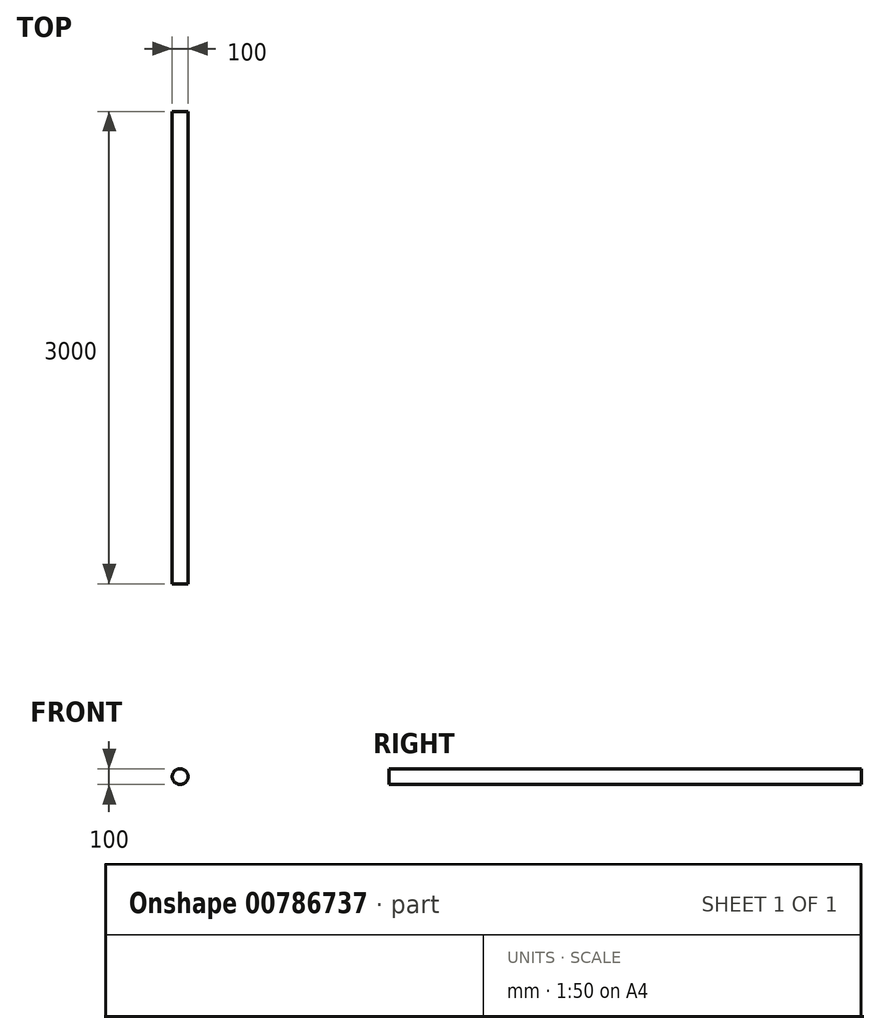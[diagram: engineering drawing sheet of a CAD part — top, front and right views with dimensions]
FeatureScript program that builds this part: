
annotation { "Feature Type Name" : "Feature", "Feature Type Description" : "" }
export const myFeature = defineFeature(function(context is Context, id is Id, definition is map)
    precondition{}
    {
        {
            var Q0;
            Q0=qCreatedBy(makeId("Front.planeOp"),FACE);
            var sketch = newSketch(context, id + "F0", { "sketchPlane" : qUnion([Q0])});
            skCircle(sketch, "E0", {"center": v(0, 0) * mm, "radius": 50 * mm});
            skSolve(sketch);
        }
        {
            var Q0;
            Q0=makeQuery(id+"F0.imprint","IMPRINT",FACE,{"disambiguationData":[TD([[makeQuery(id+"F0.imprint","IMPRINT",EDGE,{"derivedFrom":sQuery(id+"F0.wireOp",EDGE,"E0")}),1.0]])]});
            extrude(context, id + "F1", {"entities" : qUnion([Q0]), "depth" : 3000 * mm, "offsetDistance" : 25 * mm});
        }
    });
